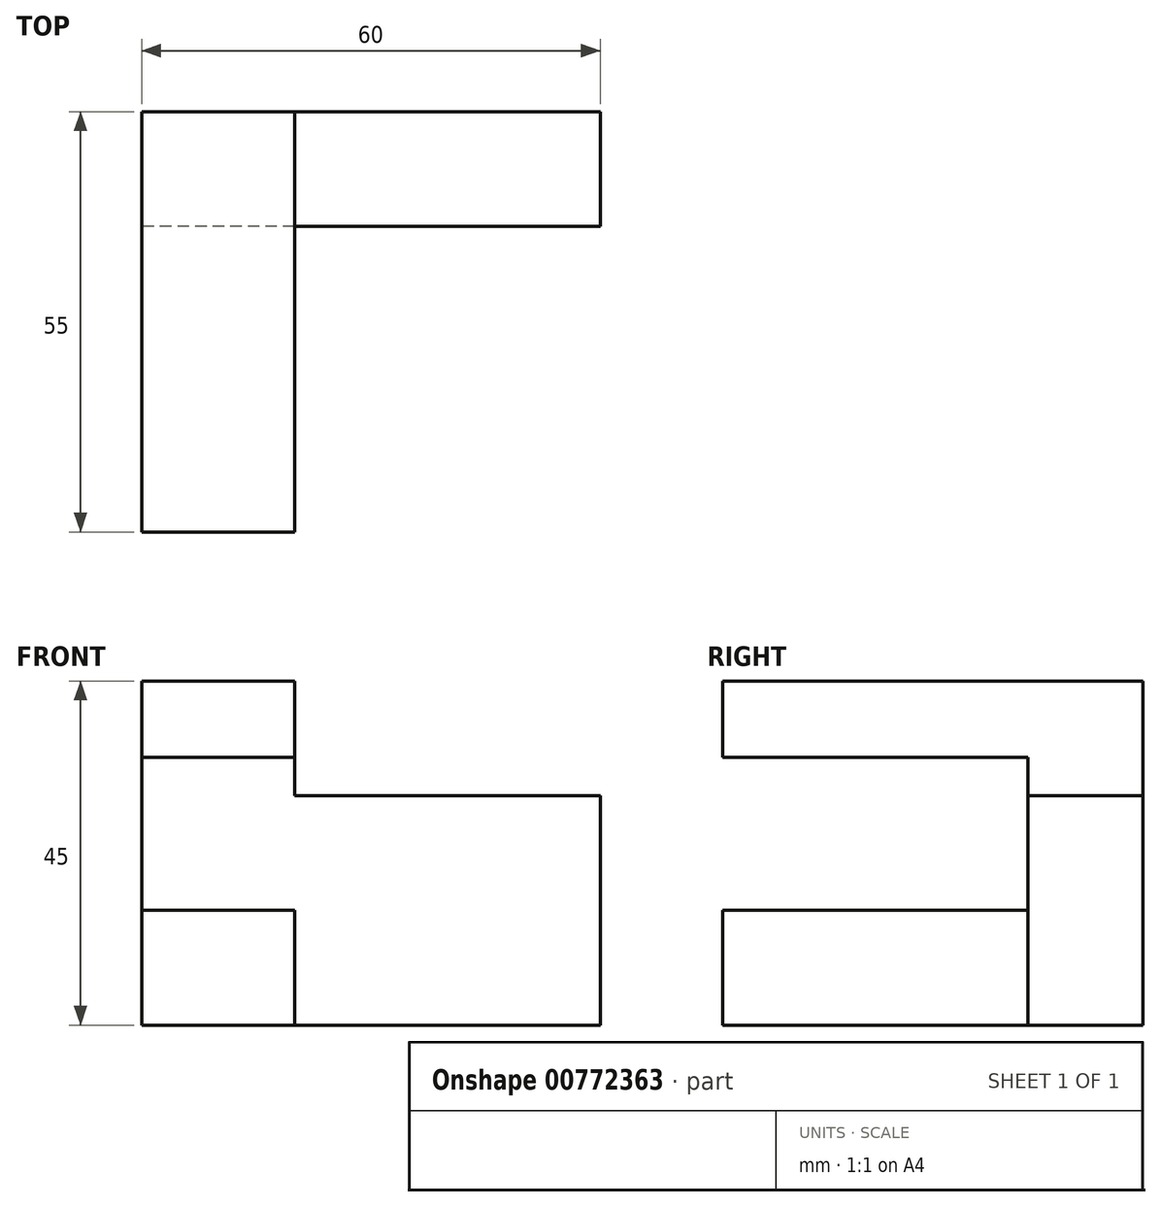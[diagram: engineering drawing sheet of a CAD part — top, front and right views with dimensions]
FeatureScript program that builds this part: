
annotation { "Feature Type Name" : "Feature", "Feature Type Description" : "" }
export const myFeature = defineFeature(function(context is Context, id is Id, definition is map)
    precondition{}
    {
        {
            var Q0;
            Q0=qCreatedBy(makeId("Front.planeOp"),FACE);
            var sketch = newSketch(context, id + "F0", { "sketchPlane" : qUnion([Q0])});
            skLineSegment(sketch, "E0.bottom", {"start": v(0, 0) * mm, "end": v(60, 0) * mm});
            skLineSegment(sketch, "E0.top", {"start": v(0, 45) * mm, "end": v(20, 45) * mm});
            skLineSegment(sketch, "E0.left", {"start": v(0, 0) * mm, "end": v(0, 45) * mm});
            skLineSegment(sketch, "E0.right", {"start": v(60, 0) * mm, "end": v(60, 30) * mm});
            skLineSegment(sketch, "E1", {"start": v(20, 30) * mm, "end": v(60, 30) * mm});
            skLineSegment(sketch, "E2", {"start": v(20, 45) * mm, "end": v(20, 35) * mm});
            skLineSegment(sketch, "E3", {"start": v(20, 35) * mm, "end": v(0, 35) * mm});
            skLineSegment(sketch, "E4", {"start": v(20, 0) * mm, "end": v(20, 15) * mm});
            skLineSegment(sketch, "E5", {"start": v(20, 15) * mm, "end": v(0, 15) * mm});
            skLineSegment(sketch, "E6", {"start": v(20, 30) * mm, "end": v(20, 35) * mm});
            skSolve(sketch);
        }
        {
            var Q0;
            Q0 = qSketchRegion(id + "F0", true);
            extrude(context, id + "F1", {"entities" : qUnion([Q0]), "oppositeDirection" : true, "depth" : 15 * mm, "offsetDistance" : 25 * mm});
        }
        {
            var Q0;
            {var subQ0=sQuery(id+"F0.wireOp",EDGE,"E0.top");Q0=makeQuery(id+"F0.imprint","IMPRINT",FACE,{"disambiguationData":[TD([[makeQuery(id+"F0.imprint","IMPRINT",EDGE,{"derivedFrom":subQ0}),-1.0]])]});}
            var Q1;
            {var subQ3=sQuery(id+"F0.wireOp",EDGE,"E4");Q1=makeQuery(id+"F0.imprint","IMPRINT",FACE,{"disambiguationData":[TD([[makeQuery(id+"F0.imprint","IMPRINT",EDGE,{"derivedFrom":subQ3}),1.0]])]});}
            extrude(context, id + "F2", {"entities" : qUnion([Q0, Q1]), "operationType" : NewBodyOperationType.ADD, "depth" : 40 * mm, "offsetDistance" : 25 * mm});
        }
    });
